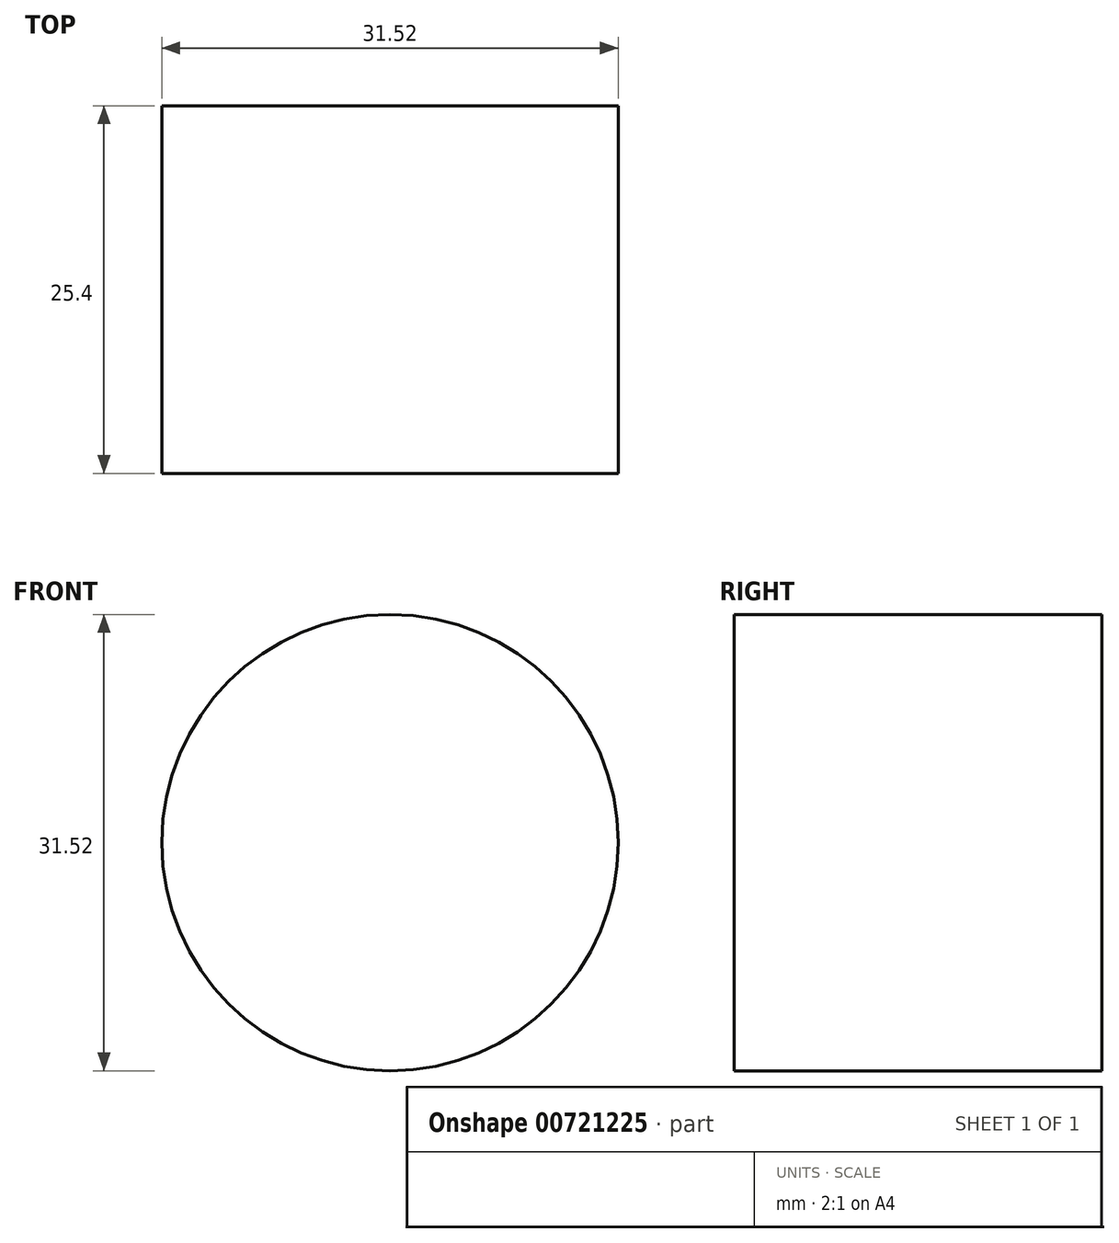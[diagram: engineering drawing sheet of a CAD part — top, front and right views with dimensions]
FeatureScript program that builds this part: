
annotation { "Feature Type Name" : "Feature", "Feature Type Description" : "" }
export const myFeature = defineFeature(function(context is Context, id is Id, definition is map)
    precondition{}
    {
        {
            var Q0;
            Q0=qCreatedBy(makeId("Front.planeOp"), FACE);
            var sketch = newSketch(context, id + "F0", { "sketchPlane" : qUnion([Q0])});
            skCircle(sketch, "E0", {"center": v(0, 0) * mm, "radius": 15.76 * mm});
            skSolve(sketch);
        }
        {
            var Q0;
            Q0 = qSketchRegion(id + "F0", true);
            extrude(context, id + "F1", {"entities" : qUnion([Q0]), "depth" : 25.4 * mm, "offsetDistance" : 25.4 * mm});
        }
    });
